# Revit family: Artemide_NurAcoustic
name_source: partatom
category: Apparecchi per illuminazione
revit_build: Autodesk Revit 2018 (Build: 20190510_1515(x64)
units: mm (PartAtom-declared; Revit-internal decimal feet)

## family parameters
Basato su piano di lavoro = Sì
Condiviso = No
Numero OmniClass = 23.80.70.00
Punto di calcolo locali = No
Quota connettore circolare = Usa diametro
Sempre verticale = Sì
Sorgente d'illuminazione = Sì
Taglio con vuoti quando caricato = No
Tipo di parte = Normale
Titolo OmniClass = Lighting

## types (5) — shared parameters
6 Monthly = -
Air Handling = -
Angolo inclinazione = 90.00°
Annually = -
Application Environment = Indoor
Beam Angle Longditudinal Axis  = 0.00°
Beam Angle Transverse Axis  = 0.00°
Bespoke Timeframe = -
CE Approval = Y
Cable Material = Stainless Steel
Colour Rendering Index = 90
Colour Temperature = 3000
Column = -
Control Gear Location = -
Control Gear Required = -
Control Gear Type = -
Daily = -
Daylight Sensor = -
Diameter_Lamp = 917 mm
Diffuser Finish = Opac
Diffuser Material  = Glass
Diffusing screen = -
ENEC Certification of European conformity = Y
Earth Point  = -
Efficacy = 76.89
Efficiency = 68
Emergency = -
Emergency Lighting Battery = -
Emetti da lunghezza linea = 610 mm
End Caps/Transition Caps/Joints = -
Environmental Product Declaration = -
Expected Life = -
Face Shape = Circular
Features = ---
Filtro dei colori = 16777215
Fire Rated = -
Fire Shroud = -
Fixing Material = Stainless Steel
Fixings = -
Green Guide for Specification = -
Hazardous Area Category = -
Hazardous Area Protection Type = -
Height_Lamp = 705 mm
Housing Finish  = Fabric
Housing Material = Methacrylate
IES Files  = https://www.artemide.com
IK Rating = -
IP Rating = IP20
IfcExportAs = IfcLightFixtureType
IfcExportType = NOTDEFINED
Infills = -
Integral Emergency Lighting Battery Type = -
Integral Fuse or Circuit Protection  = -
Intended Market = Unset
International Type Code = -
LED lifetime = 50000
Lamp Cap = -
Lamp Included = Y
Lamp Replacement Interval = -
Lamp Survival Factor = -
Life Cycle Analysis = -
Light Fixture Mounting Type = Suspended
Light Output Pattern = Direct
Location of Manufacturer = -
Louvre/Lens = -
Luminaire Cleaning Interval  = -
Luminaire Type = Downlight
M_Diffuser = Artemide_Glass_Clear
M_Fixings = Artemide_Aluminum_Anodized
M_Reflector = Artemide_Plastic_PET
M_TopClosing = Artemide_Glass_Frosted
Maintenance Required: 0-300hrs  = -
Maintenance Required: 1001-2000hrs  = -
Maintenance Required: 2001-4000hrs  = -
Maintenance Required: 301-600hrs  = -
Maintenance Required: 4001-8000hrs  = -
Maintenance Required: 601-1000hrs = -
Maintenance Required: 8001-12000hrs  = -
Manufacturer Website = https://www.artemide.com
Material Ingredient Reporting = -
Max Height from ceiling = 2600 mm
Modello = Nur Acoustic
Monthly = -
Motion Sensor = -
Number of Primary Lamps = 1
Overall Height = 705 mm
Overall Length = 917 mm
Photocell = -
Power Supply Kit = -
Primary Lamp Type = LED
Product Literature = https://www.artemide.com
Product Range = Nur Acoustic
Produttore = Artemide
Prospetto di default = 1219 mm
Quarterly = -
Reflector Finish = Opac acrylic
Reflector Material = PET
Responsible Extraction of Materials = -
Responsible Sourcing of Materials = -
Secondary Lamp = N
Secondary Lamp Cap = -
Secondary Lamp Included = -
Secondary Lamp International Type Code = -
Service life  = -
Standards = -
Suitable Dimmer Type = -
Suitable for Dimming  = -
Suitable for Motion Detector Control = -
Suitable for Photocell Control = -
Testing method = -
URL = https://www.artemide.com
URL to Energy Technology List = -
URL to O&M Manual = https://www.artemide.com
Uniclass2015 = Pr_70_70_48
Unified Glare Rating  = -
Variazione temperatura colore lampada con luminosità attenuata = <Nessuno>
Voltage = 220
Warranty ID = https://cloud.artemide.com
Wattage  = 80
Weekly = -
zero-valued in all types: Access Clearance Bottom, Access Clearance Front, Access Clearance Left, Access Clearance Rear, Access Clearance Right, Access Clearance Top, Ambient Temperature                            , Basis of lifetime lumen depreciation  , Basis of lifetime luminaire failures       , Control Gear Standby Power , Current , Cut Out Length, Cut Out Width, Downward Component, Drive Current                                         , Duration of Integral Emergency Lighting , Embodied Carbon , Emergency Charging Power      , Emergency light output percentage, External Control Line Voltage, Face Length, Face Width, Fire Rated Temperature, Fire Rating Duration, Frequency , Gross Weight, Initial Lumens, Input Lumens Direct light, Input Lumens Indirect light, LED Initial Colour Variation                     , LED Maintained Colour Variation        , Luminaire Maintenance Factor, Luminance at 65deg Angle, Maximum Operating Temperature, Minimum Operating Temperature, Number of Poles, Number of Secondary Lamps, Output Lumens Direct light, Output Lumens Indirect light, Overall Light Output Ratio, Overall Width, Power Factor, Rated Lamp Life, Secondary Lamp Colour Rendering Index, Secondary Lamp Colour Temperature, Secondary Lamp Efficacy, Secondary Lamp Initial Lumens , Secondary Lamp Voltage, Secondary Rated Lamp Life, Shipping Weight, Supply Phase, Total Light Output , Total Power, Upward Component 

## per-type parameters (varying)
| type | File diagramma fotometrico | Housing Colour  | M_Housing | Product Model Number |
| NurAcoustic_White_A243720 | A243720.ies | White | Artemide_Fabric_White | A243720 |
| NurAcoustic_Blue_A243750 | A243750.ies | Blue | Artemide_Fabric_Blue | A243750 |
| NurAcoustic_Grey_A243700 | A243700.ies | Grey | Artemide_Fabric_Grey | A243700 |
| NurAcoustic_Red_A243740 | A243740.ies | Red | Artemide_Fabric_Red | A243740 |
| NurAcoustic_Green_A243770 | A243770.ies | Green | Artemide_Fabric_Green | A243770 |

## geometry (parser evidence)
native form markers: Sweep x3
no freeform markers — native parametric forms only
